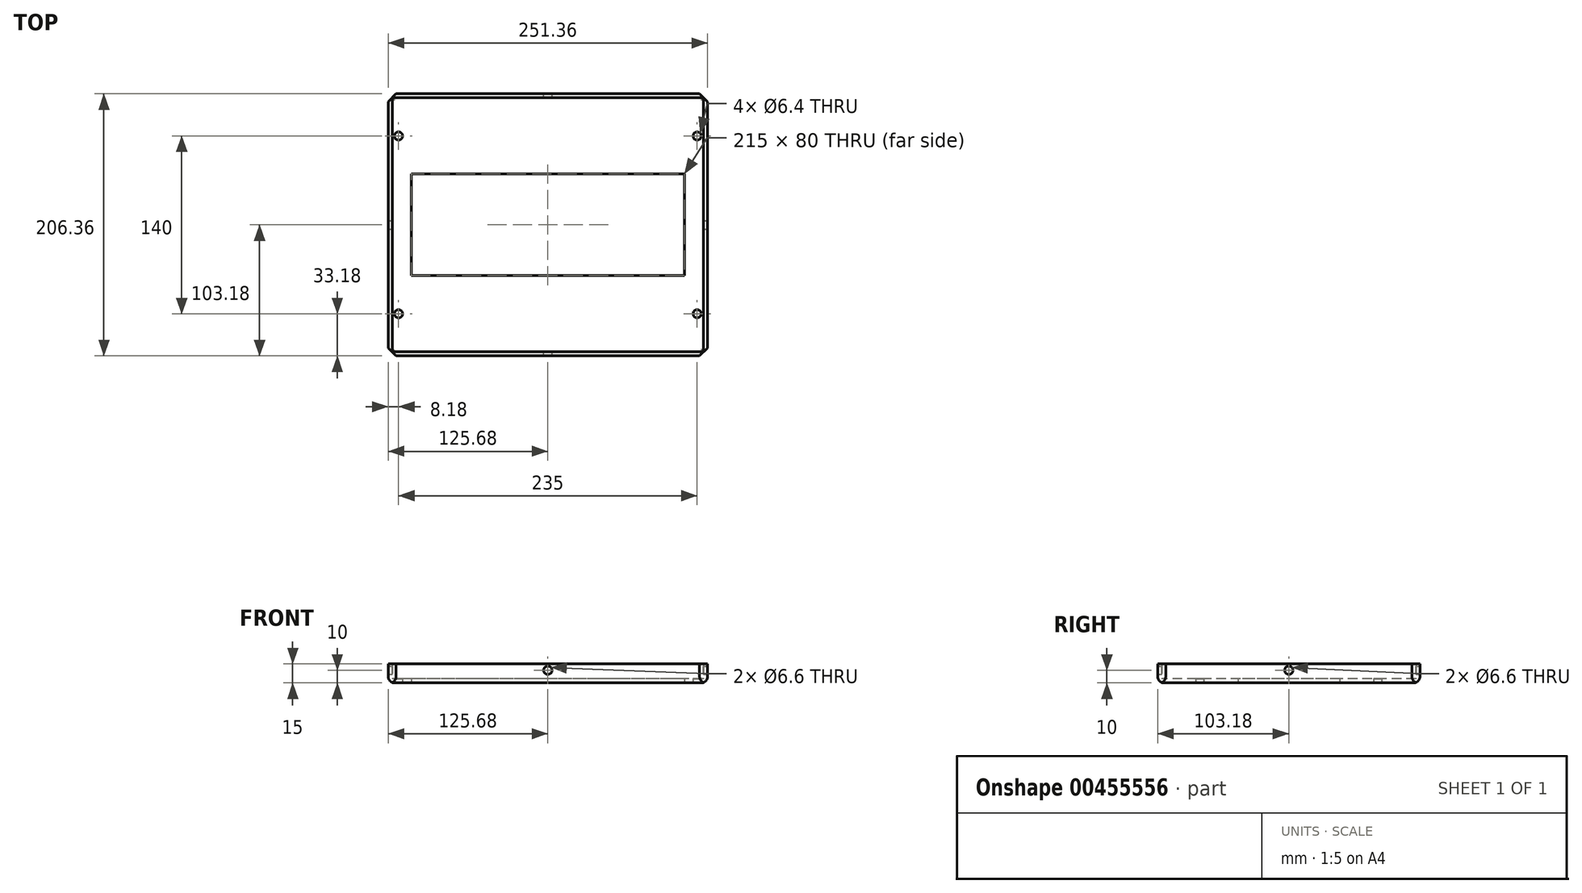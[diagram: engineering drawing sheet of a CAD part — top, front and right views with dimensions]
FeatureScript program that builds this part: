
annotation { "Feature Type Name" : "Feature", "Feature Type Description" : "" }
export const myFeature = defineFeature(function(context is Context, id is Id, definition is map)
    precondition{}
    {
        {
            var Q0;
            Q0=qCreatedBy(makeId("Top.planeOp"),FACE);
            var sketch = newSketch(context, id + "F0", { "sketchPlane" : qUnion([Q0])});
            skLineSegment(sketch, "E0.bottom", {"start": v(122.5, 100) * mm, "end": v(-122.5, 100) * mm});
            skLineSegment(sketch, "E0.top", {"start": v(122.5, -100) * mm, "end": v(-122.5, -100) * mm});
            skLineSegment(sketch, "E0.left", {"start": v(122.5, 100) * mm, "end": v(122.5, -100) * mm});
            skLineSegment(sketch, "E0.right", {"start": v(-122.5, 100) * mm, "end": v(-122.5, -100) * mm});
            skPoint(sketch, "E0.middle", {"position": v(0, 0) * mm});
            skCircle(sketch, "E1", {"center": v(-117.5, 70) * mm, "radius": 3.2 * mm});
            skCircle(sketch, "E2", {"center": v(117.5, 70) * mm, "radius": 3.2 * mm});
            skCircle(sketch, "E3.MirrorC", {"center": v(-117.5, -70) * mm, "radius": 3.2 * mm});
            skCircle(sketch, "E4.MirrorC", {"center": v(117.5, -70) * mm, "radius": 3.2 * mm});
            skLineSegment(sketch, "E5.bottom", {"start": v(107.5, 40) * mm, "end": v(-107.5, 40) * mm});
            skLineSegment(sketch, "E5.top", {"start": v(107.5, -40) * mm, "end": v(-107.5, -40) * mm});
            skLineSegment(sketch, "E5.left", {"start": v(107.5, 40) * mm, "end": v(107.5, -40) * mm});
            skLineSegment(sketch, "E5.right", {"start": v(-107.5, 40) * mm, "end": v(-107.5, -40) * mm});
            skSolve(sketch);
        }
        {
            var Q0;
            Q0=makeQuery(id+"F0.imprint","IMPRINT",FACE,{"disambiguationData":[TD([[makeQuery(id+"F0.imprint","IMPRINT",EDGE,{"derivedFrom":sQuery(id+"F0.wireOp",EDGE,"E0.bottom")}),1.0]])]});
            extrude(context, id + "F1", {"entities" : qUnion([Q0]), "depth" : 3.17 * mm});
        }
        {
            var Q0;
            Q0=makeQuery(id+"F1.opExtrude","CAP_FACE",FACE,{"disambiguationData":[OSD([sQuery(id+"F0.wireOp",EDGE,"E0.bottom"),sQuery(id+"F0.wireOp",EDGE,"E0.top"),sQuery(id+"F0.wireOp",EDGE,"E0.left"),sQuery(id+"F0.wireOp",EDGE,"E0.right"),sQuery(id+"F0.wireOp",EDGE,"E1"),sQuery(id+"F0.wireOp",EDGE,"E2"),sQuery(id+"F0.wireOp",EDGE,"E3.MirrorC"),sQuery(id+"F0.wireOp",EDGE,"E4.MirrorC"),sQuery(id+"F0.wireOp",EDGE,"E5.bottom"),sQuery(id+"F0.wireOp",EDGE,"E5.top"),sQuery(id+"F0.wireOp",EDGE,"E5.left"),sQuery(id+"F0.wireOp",EDGE,"E5.right")])],"isStart":true});
            var sketch = newSketch(context, id + "F2", { "sketchPlane" : qUnion([Q0])});
            skLineSegment(sketch, "E6.0", {"start": v(125.67, -103.18) * mm, "end": v(125.67, 103.17) * mm});
            skLineSegment(sketch, "E6.1", {"start": v(125.67, -103.18) * mm, "end": v(-125.68, -103.18) * mm});
            skLineSegment(sketch, "E6.2", {"start": v(-125.68, -103.17) * mm, "end": v(-125.68, 103.17) * mm});
            skLineSegment(sketch, "E6.3", {"start": v(125.67, 103.17) * mm, "end": v(-125.68, 103.17) * mm});
            skLineSegment(sketch, "E7.bottom", {"start": v(122.5, 100) * mm, "end": v(-122.5, 100) * mm});
            skLineSegment(sketch, "E7.top", {"start": v(122.5, -100) * mm, "end": v(-122.5, -100) * mm});
            skLineSegment(sketch, "E7.left", {"start": v(122.5, 100) * mm, "end": v(122.5, -100) * mm});
            skLineSegment(sketch, "E7.right", {"start": v(-122.5, 100) * mm, "end": v(-122.5, -100) * mm});
            skSolve(sketch);
        }
        {
            var Q0;
            Q0 = qSketchRegion(id + "F2", true);
            extrude(context, id + "F3", {"entities" : qUnion([Q0]), "operationType" : NewBodyOperationType.ADD, "oppositeDirection" : true, "depth" : 15 * mm});
        }
        {
            var Q0;
            Q0=makeQuery(id+"F3.opExtrude","SWEPT_EDGE",EDGE,{"disambiguationData":[OSD([sQuery(id+"F2.wireOp",EDGE,"E6.1"),sQuery(id+"F2.wireOp",EDGE,"E6.2")])]});
            var Q1;
            Q1=makeQuery(id+"F3.opExtrude","SWEPT_EDGE",EDGE,{"disambiguationData":[OSD([sQuery(id+"F2.wireOp",EDGE,"E6.0"),sQuery(id+"F2.wireOp",EDGE,"E6.1")])]});
            var Q2;
            Q2=makeQuery(id+"F3.opExtrude","SWEPT_EDGE",EDGE,{"disambiguationData":[OSD([sQuery(id+"F2.wireOp",EDGE,"E6.0"),sQuery(id+"F2.wireOp",EDGE,"E6.3")])]});
            var Q3;
            Q3=makeQuery(id+"F3.opExtrude","SWEPT_EDGE",EDGE,{"disambiguationData":[OSD([sQuery(id+"F2.wireOp",EDGE,"E6.2"),sQuery(id+"F2.wireOp",EDGE,"E6.3")])]});
            chamfer(context, id + "F4", {"entities" : qUnion([Q0, Q1, Q2, Q3]), "width" : 6.3 * mm, "tangentPropagation" : true});
        }
        {
            var Q0;
            Q0=makeQuery(id+"F3.opExtrude","SWEPT_FACE",FACE,{"disambiguationData":[OSD([sQuery(id+"F2.wireOp",EDGE,"E6.0")])]});
            var sketch = newSketch(context, id + "F5", { "sketchPlane" : qUnion([Q0])});
            skSolve(sketch);
        }
        {
            var Q0;
            {var subQ0=sQuery(id+"F2.wireOp",EDGE,"E6.0");Q0=makeQuery(id+"F5.imprint","IMPRINT",FACE,{"disambiguationData":[TD([[makeQuery(id+"F5.imprint","IMPRINT",EDGE,{"derivedFrom":makeQuery(id+"F3.opExtrude","CAP_EDGE",EDGE,{"disambiguationData":[OSD([subQ0])],"isStart":true})}),-1.0]])]});}
            var sketch = newSketch(context, id + "F6", { "sketchPlane" : qUnion([Q0])});
            skCircle(sketch, "E8", {"center": v(0, 10) * mm, "radius": 3.3 * mm});
            skSolve(sketch);
        }
        {
            var Q0;
            Q0 = qSketchRegion(id + "F6", true);
            extrude(context, id + "F7", {"entities" : qUnion([Q0]), "operationType" : NewBodyOperationType.REMOVE, "endBound" : BoundingType.THROUGH_ALL, "oppositeDirection" : true, "depth" : 25 * mm});
        }
        {
            var Q0;
            Q0=makeQuery(id+"F3.opExtrude","SWEPT_FACE",FACE,{"disambiguationData":[OSD([sQuery(id+"F2.wireOp",EDGE,"E6.1")])]});
            var sketch = newSketch(context, id + "F8", { "sketchPlane" : qUnion([Q0])});
            skCircle(sketch, "E9", {"center": v(0, 10) * mm, "radius": 3.3 * mm});
            skSolve(sketch);
        }
        {
            var Q0;
            Q0 = qSketchRegion(id + "F8", true);
            extrude(context, id + "F9", {"entities" : qUnion([Q0]), "operationType" : NewBodyOperationType.REMOVE, "endBound" : BoundingType.THROUGH_ALL, "oppositeDirection" : true, "depth" : 25 * mm});
        }
        {
            var Q0;
            Q0=makeQuery(id+"F3.opExtrude","CAP_EDGE",EDGE,{"disambiguationData":[OSD([sQuery(id+"F2.wireOp",EDGE,"E6.3")])],"isStart":true});
            var Q1;
            Q1=makeQuery(id+"F3.opExtrude","CAP_EDGE",EDGE,{"disambiguationData":[OSD([sQuery(id+"F2.wireOp",EDGE,"E6.2")])],"isStart":true});
            var Q2;
            Q2=makeQuery(id+"F3.opExtrude","CAP_EDGE",EDGE,{"disambiguationData":[OSD([sQuery(id+"F2.wireOp",EDGE,"E6.1")])],"isStart":true});
            var Q3;
            Q3=makeQuery(id+"F3.opExtrude","CAP_EDGE",EDGE,{"disambiguationData":[OSD([sQuery(id+"F2.wireOp",EDGE,"E6.0")])],"isStart":true});
            fillet(context, id + "F10", {"entities" : qUnion([Q0, Q1, Q2, Q3]), "radius" : 5 * mm, "tangentPropagation" : true, "allowEdgeOverflow" : false});
        }
    });
